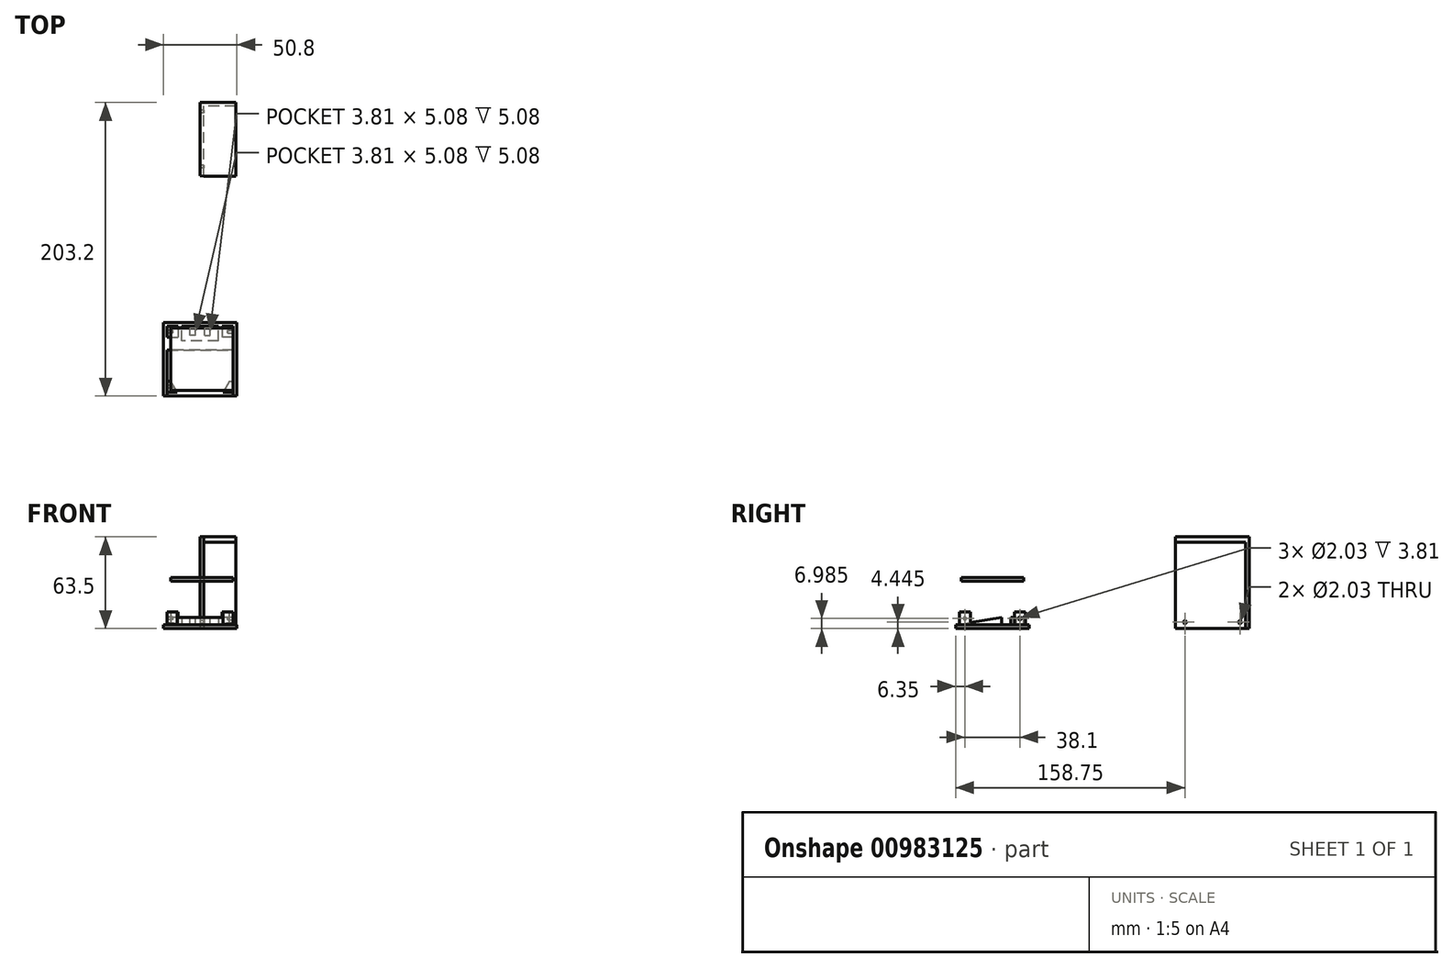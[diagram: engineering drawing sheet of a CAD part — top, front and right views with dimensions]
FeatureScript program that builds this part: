
annotation { "Feature Type Name" : "Feature", "Feature Type Description" : "" }
export const myFeature = defineFeature(function(context is Context, id is Id, definition is map)
    precondition{}
    {
        {
            var Q0;
            Q0=qCreatedBy(makeId("Top.planeOp"),FACE);
            var sketch = newSketch(context, id + "F0", { "sketchPlane" : qUnion([Q0])});
            skLineSegment(sketch, "E0.bottom", {"start": v(25.4, 25.4) * mm, "end": v(-25.4, 25.4) * mm});
            skLineSegment(sketch, "E0.top", {"start": v(25.4, -25.4) * mm, "end": v(-25.4, -25.4) * mm});
            skLineSegment(sketch, "E0.left", {"start": v(25.4, 25.4) * mm, "end": v(25.4, -25.4) * mm});
            skLineSegment(sketch, "E0.right", {"start": v(-25.4, 25.4) * mm, "end": v(-25.4, -25.4) * mm});
            skPoint(sketch, "E0.middle", {"position": v(0, 0) * mm});
            skSolve(sketch);
        }
        {
            var Q0;
            Q0=makeQuery(id+"F0.imprint","IMPRINT",FACE,{"disambiguationData":[TD([[makeQuery(id+"F0.imprint","IMPRINT",EDGE,{"derivedFrom":sQuery(id+"F0.wireOp",EDGE,"E0.bottom")}),1.0]])]});
            extrude(context, id + "F1", {"entities" : qUnion([Q0]), "depth" : 2.54 * mm, "offsetDistance" : 25.4 * mm});
        }
        {
            var Q0;
            Q0=makeQuery(id+"F1.opExtrude","CAP_FACE",FACE,{"disambiguationData":[OSD([sQuery(id+"F0.wireOp",EDGE,"E0.bottom"),sQuery(id+"F0.wireOp",EDGE,"E0.top"),sQuery(id+"F0.wireOp",EDGE,"E0.left"),sQuery(id+"F0.wireOp",EDGE,"E0.right")])],"isStart":false});
            var sketch = newSketch(context, id + "F2", { "sketchPlane" : qUnion([Q0])});
            skLineSegment(sketch, "E1", {"start": v(0, 25.4) * mm, "end": v(0, 12.7) * mm});
            skLineSegment(sketch, "E2.bottom", {"start": v(0, 12.7) * mm, "end": v(12.7, 12.7) * mm});
            skLineSegment(sketch, "E2.top", {"start": v(0, 25.4) * mm, "end": v(12.7, 25.4) * mm});
            skLineSegment(sketch, "E2.left", {"start": v(0, 12.7) * mm, "end": v(0, 25.4) * mm});
            skLineSegment(sketch, "E2.right", {"start": v(12.7, 12.7) * mm, "end": v(12.7, 25.4) * mm});
            skLineSegment(sketch, "E3.bottom", {"start": v(0, 12.7) * mm, "end": v(-12.7, 12.7) * mm});
            skLineSegment(sketch, "E3.top", {"start": v(0, 25.4) * mm, "end": v(-12.7, 25.4) * mm});
            skLineSegment(sketch, "E3.right", {"start": v(-12.7, 12.7) * mm, "end": v(-12.7, 25.4) * mm});
            skSolve(sketch);
        }
        {
            var Q0;
            Q0=makeQuery(id+"F2.imprint","IMPRINT",FACE,{"disambiguationData":[TD([[makeQuery(id+"F2.imprint","IMPRINT",EDGE,{"derivedFrom":sQuery(id+"F2.wireOp",EDGE,"E3.bottom")}),-1.0]])]});
            var Q1;
            Q1=makeQuery(id+"F2.imprint","IMPRINT",FACE,{"disambiguationData":[TD([[makeQuery(id+"F2.imprint","IMPRINT",EDGE,{"derivedFrom":sQuery(id+"F2.wireOp",EDGE,"E2.bottom")}),1.0]])]});
            extrude(context, id + "F3", {"entities" : qUnion([Q0, Q1]), "operationType" : NewBodyOperationType.ADD, "depth" : 5.08 * mm, "offsetDistance" : 25.4 * mm});
        }
        {
            var Q0;
            Q0=makeQuery(id+"F3.opExtrude","CAP_FACE",FACE,{"disambiguationData":[OSD([sQuery(id+"F2.wireOp",EDGE,"E2.bottom"),sQuery(id+"F2.wireOp",EDGE,"E2.top"),sQuery(id+"F2.wireOp",EDGE,"E2.right"),sQuery(id+"F2.wireOp",EDGE,"E3.bottom"),sQuery(id+"F2.wireOp",EDGE,"E3.top"),sQuery(id+"F2.wireOp",EDGE,"E3.right")])],"isStart":false});
            var sketch = newSketch(context, id + "F4", { "sketchPlane" : qUnion([Q0])});
            skLineSegment(sketch, "E4", {"start": v(0, 25.4) * mm, "end": v(0, 16.51) * mm, "construction": true});
            skPoint(sketch, "E4.endSnap0", {"position": v(0, 12.7) * mm});
            skLineSegment(sketch, "E5", {"start": v(0, 16.51) * mm, "end": v(-3.17, 16.51) * mm, "construction": true});
            skLineSegment(sketch, "E6.bottom", {"start": v(-3.17, 16.51) * mm, "end": v(-6.99, 16.51) * mm});
            skLineSegment(sketch, "E6.top", {"start": v(-3.18, 21.6) * mm, "end": v(-6.99, 21.6) * mm});
            skLineSegment(sketch, "E6.left", {"start": v(-3.18, 16.51) * mm, "end": v(-3.18, 21.6) * mm});
            skLineSegment(sketch, "E6.right", {"start": v(-6.98, 16.51) * mm, "end": v(-6.99, 21.6) * mm});
            skLineSegment(sketch, "E7.MirrorCS", {"start": v(0, 16.51) * mm, "end": v(3.18, 16.51) * mm, "construction": true});
            skLineSegment(sketch, "E8.MirrorCS", {"start": v(3.18, 16.51) * mm, "end": v(3.18, 21.6) * mm});
            skLineSegment(sketch, "E9.MirrorCS", {"start": v(3.18, 21.6) * mm, "end": v(6.99, 21.6) * mm});
            skLineSegment(sketch, "E10.MirrorCS", {"start": v(6.99, 16.51) * mm, "end": v(6.99, 21.6) * mm});
            skLineSegment(sketch, "E11.MirrorCS", {"start": v(3.18, 16.51) * mm, "end": v(6.99, 16.51) * mm});
            skSolve(sketch);
        }
        {
            var Q0;
            Q0=makeQuery(id+"F4.imprint","IMPRINT",FACE,{"disambiguationData":[TD([[makeQuery(id+"F4.imprint","IMPRINT",EDGE,{"derivedFrom":sQuery(id+"F4.wireOp",EDGE,"E6.bottom")}),-1.0]])]});
            var Q1;
            Q1=makeQuery(id+"F4.imprint","IMPRINT",FACE,{"disambiguationData":[TD([[makeQuery(id+"F4.imprint","IMPRINT",EDGE,{"derivedFrom":sQuery(id+"F4.wireOp",EDGE,"E8.MirrorCS")}),-1.0]])]});
            extrude(context, id + "F5", {"entities" : qUnion([Q0, Q1]), "operationType" : NewBodyOperationType.REMOVE, "oppositeDirection" : true, "depth" : 5.08 * mm, "offsetDistance" : 25.4 * mm});
        }
        {
            var Q0;
            Q0=makeQuery(id+"F1.opExtrude","CAP_FACE",FACE,{"disambiguationData":[OSD([sQuery(id+"F0.wireOp",EDGE,"E0.bottom"),sQuery(id+"F0.wireOp",EDGE,"E0.top"),sQuery(id+"F0.wireOp",EDGE,"E0.left"),sQuery(id+"F0.wireOp",EDGE,"E0.right")])],"isStart":false});
            var sketch = newSketch(context, id + "F6", { "sketchPlane" : qUnion([Q0])});
            skLineSegment(sketch, "E12", {"start": v(-25.4, 22.86) * mm, "end": v(-22.86, 22.86) * mm});
            skLineSegment(sketch, "E13", {"start": v(-22.86, 22.86) * mm, "end": v(-22.86, 25.4) * mm});
            skLineSegment(sketch, "E14.MirrorCS", {"start": v(-25.4, -22.86) * mm, "end": v(-22.86, -22.86) * mm});
            skLineSegment(sketch, "E15.MirrorCS", {"start": v(-22.86, -22.86) * mm, "end": v(-22.86, -25.4) * mm});
            skLineSegment(sketch, "E16.MirrorCS", {"start": v(22.86, 22.86) * mm, "end": v(22.86, 25.4) * mm});
            skLineSegment(sketch, "E17.MirrorCS", {"start": v(25.4, 22.86) * mm, "end": v(22.86, 22.86) * mm});
            skLineSegment(sketch, "E18.MirrorCS", {"start": v(25.4, -22.86) * mm, "end": v(22.86, -22.86) * mm});
            skLineSegment(sketch, "E19.MirrorCS", {"start": v(22.86, -22.86) * mm, "end": v(22.86, -25.4) * mm});
            skLineSegment(sketch, "E20.bottom", {"start": v(-22.86, 22.86) * mm, "end": v(-15.24, 22.86) * mm});
            skLineSegment(sketch, "E20.top", {"start": v(-22.86, 15.24) * mm, "end": v(-15.24, 15.24) * mm});
            skLineSegment(sketch, "E20.left", {"start": v(-22.86, 22.86) * mm, "end": v(-22.86, 15.24) * mm});
            skLineSegment(sketch, "E20.right", {"start": v(-15.24, 22.86) * mm, "end": v(-15.24, 15.24) * mm});
            skLineSegment(sketch, "E21.MirrorCS", {"start": v(22.86, 22.86) * mm, "end": v(15.24, 22.86) * mm});
            skLineSegment(sketch, "E22.MirrorCS", {"start": v(15.24, 22.86) * mm, "end": v(15.24, 15.24) * mm});
            skLineSegment(sketch, "E23.MirrorCS", {"start": v(22.86, 22.86) * mm, "end": v(22.86, 15.24) * mm});
            skLineSegment(sketch, "E24.MirrorCS", {"start": v(22.86, 15.24) * mm, "end": v(15.24, 15.24) * mm});
            skLineSegment(sketch, "E25.bottom", {"start": v(-22.86, -25.4) * mm, "end": v(22.86, -25.4) * mm});
            skLineSegment(sketch, "E25.top", {"start": v(-22.86, 6.35) * mm, "end": v(22.86, 6.35) * mm});
            skLineSegment(sketch, "E25.left", {"start": v(-22.86, -25.4) * mm, "end": v(-22.86, 6.35) * mm});
            skLineSegment(sketch, "E25.right", {"start": v(22.86, -25.4) * mm, "end": v(22.86, 6.35) * mm});
            skLineSegment(sketch, "E26.MirrorCS", {"start": v(-22.86, -22.86) * mm, "end": v(-22.86, -15.24) * mm});
            skLineSegment(sketch, "E27.MirrorCS", {"start": v(22.86, -22.86) * mm, "end": v(22.86, -15.24) * mm});
            skLineSegment(sketch, "E28.MirrorCS", {"start": v(22.86, -22.86) * mm, "end": v(15.24, -22.86) * mm});
            skLineSegment(sketch, "E29.MirrorCS", {"start": v(22.86, -15.24) * mm, "end": v(15.24, -15.24) * mm});
            skLineSegment(sketch, "E30.MirrorCS", {"start": v(15.24, -22.86) * mm, "end": v(15.24, -15.24) * mm});
            skLineSegment(sketch, "E31.MirrorCS", {"start": v(-22.86, -15.24) * mm, "end": v(-15.24, -15.24) * mm});
            skLineSegment(sketch, "E32.MirrorCS", {"start": v(-15.24, -22.86) * mm, "end": v(-15.24, -15.24) * mm});
            skLineSegment(sketch, "E33.MirrorCS", {"start": v(-22.86, -22.86) * mm, "end": v(-15.24, -22.86) * mm});
            skSolve(sketch);
        }
        {
            var Q0;
            Q0=makeQuery(id+"F6.imprint","IMPRINT",FACE,{"disambiguationData":[TD([[makeQuery(id+"F6.imprint","IMPRINT",EDGE,{"derivedFrom":sQuery(id+"F6.wireOp",EDGE,"E20.bottom")}),-1.0]])]});
            var Q1;
            Q1=makeQuery(id+"F6.imprint","IMPRINT",FACE,{"disambiguationData":[TD([[makeQuery(id+"F6.imprint","IMPRINT",EDGE,{"derivedFrom":sQuery(id+"F6.wireOp",EDGE,"E21.MirrorCS")}),1.0]])]});
            var Q2;
            {var subQ3=sQuery(id+"F6.wireOp",EDGE,"E25.bottom");Q2=makeQuery(id+"F6.imprint","IMPRINT",FACE,{"disambiguationData":[TD([[makeQuery(id+"F6.imprint","IMPRINT",EDGE,{"derivedFrom":subQ3}),-1.0]])]});}
            extrude(context, id + "F7", {"entities" : qUnion([Q0, Q1, Q2]), "operationType" : NewBodyOperationType.ADD, "depth" : 8.9 * mm, "offsetDistance" : 25.4 * mm});
        }
        {
            var Q0;
            Q0=makeQuery(id+"F7.opExtrude","CAP_EDGE",EDGE,{"disambiguationData":[OSD([sQuery(id+"F6.wireOp",EDGE,"E25.bottom")])],"isStart":false});
            chamfer(context, id + "F8", {"entities" : qUnion([Q0]), "chamferType" : ChamferType.OFFSET_ANGLE, "width" : 8.9 * mm, "oppositeDirection" : false, "angle" : 81 * degree, "tangentPropagation" : true});
        }
        {
            var Q0;
            Q0=qCreatedBy(makeId("Top.planeOp"),FACE);
            var sketch = newSketch(context, id + "F9", { "sketchPlane" : qUnion([Q0])});
            skLineSegment(sketch, "E34", {"start": v(0, 0) * mm, "end": v(0, 127) * mm, "construction": true});
            skLineSegment(sketch, "E35", {"start": v(0, 127) * mm, "end": v(0, 177.8) * mm});
            skLineSegment(sketch, "E36", {"start": v(0, 177.8) * mm, "end": v(24.64, 177.8) * mm});
            skLineSegment(sketch, "E37", {"start": v(24.64, 177.8) * mm, "end": v(24.64, 175.26) * mm});
            skLineSegment(sketch, "E38", {"start": v(24.64, 175.26) * mm, "end": v(2.54, 175.26) * mm});
            skLineSegment(sketch, "E39", {"start": v(2.54, 175.26) * mm, "end": v(2.54, 126.89) * mm});
            skLineSegment(sketch, "E40", {"start": v(2.54, 126.89) * mm, "end": v(0, 127) * mm});
            skSolve(sketch);
        }
        {
            var Q0;
            Q0=makeQuery(id+"F9.imprint","IMPRINT",FACE,{"disambiguationData":[TD([[makeQuery(id+"F9.imprint","IMPRINT",EDGE,{"derivedFrom":sQuery(id+"F9.wireOp",EDGE,"E35")}),-1.0]])]});
            extrude(context, id + "F10", {"entities" : qUnion([Q0]), "depth" : 63.5 * mm, "offsetDistance" : 25.4 * mm});
        }
        {
            var Q0;
            Q0=makeQuery(id+"F10.opExtrude","SWEPT_FACE",FACE,{"disambiguationData":[OSD([sQuery(id+"F9.wireOp",EDGE,"E39")])]});
            var sketch = newSketch(context, id + "F11", { "sketchPlane" : qUnion([Q0])});
            skLineSegment(sketch, "E41", {"start": v(126.89, 63.5) * mm, "end": v(126.89, 59.69) * mm});
            skLineSegment(sketch, "E42.bottom", {"start": v(126.89, 59.69) * mm, "end": v(175.26, 59.69) * mm});
            skLineSegment(sketch, "E42.top", {"start": v(126.89, 63.5) * mm, "end": v(175.26, 63.5) * mm});
            skLineSegment(sketch, "E42.left", {"start": v(126.89, 59.69) * mm, "end": v(126.89, 63.5) * mm});
            skLineSegment(sketch, "E42.right", {"start": v(175.26, 59.69) * mm, "end": v(175.26, 63.5) * mm});
            skSolve(sketch);
        }
        {
            var Q0;
            Q0=makeQuery(id+"F11.imprint","IMPRINT",FACE,{"disambiguationData":[TD([[makeQuery(id+"F11.imprint","IMPRINT",EDGE,{"derivedFrom":sQuery(id+"F11.wireOp",EDGE,"E42.bottom")}),1.0]])]});
            extrude(context, id + "F12", {"entities" : qUnion([Q0]), "operationType" : NewBodyOperationType.ADD, "depth" : 22.1 * mm, "offsetDistance" : 25.4 * mm});
        }
        {
            var Q0;
            Q0=makeQuery(id+"F1.opExtrude","CAP_FACE",FACE,{"disambiguationData":[OSD([sQuery(id+"F0.wireOp",EDGE,"E0.bottom"),sQuery(id+"F0.wireOp",EDGE,"E0.top"),sQuery(id+"F0.wireOp",EDGE,"E0.left"),sQuery(id+"F0.wireOp",EDGE,"E0.right")])],"isStart":false});
            var sketch = newSketch(context, id + "F13", { "sketchPlane" : qUnion([Q0])});
            skLineSegment(sketch, "E43.bottom", {"start": v(-15.24, -15.24) * mm, "end": v(-22.86, -15.24) * mm});
            skLineSegment(sketch, "E43.top", {"start": v(-15.24, -22.86) * mm, "end": v(-22.86, -22.86) * mm});
            skLineSegment(sketch, "E43.left", {"start": v(-15.24, -15.24) * mm, "end": v(-15.24, -22.86) * mm});
            skLineSegment(sketch, "E43.right", {"start": v(-22.86, -15.24) * mm, "end": v(-22.86, -22.86) * mm});
            skLineSegment(sketch, "E44.bottom", {"start": v(15.24, -15.24) * mm, "end": v(22.86, -15.24) * mm});
            skLineSegment(sketch, "E44.top", {"start": v(15.24, -22.86) * mm, "end": v(22.86, -22.86) * mm});
            skLineSegment(sketch, "E44.left", {"start": v(15.24, -15.24) * mm, "end": v(15.24, -22.86) * mm});
            skLineSegment(sketch, "E44.right", {"start": v(22.86, -15.24) * mm, "end": v(22.86, -22.86) * mm});
            skSolve(sketch);
        }
        {
            var Q0;
            Q0=makeQuery(id+"F13.imprint","IMPRINT",FACE,{"disambiguationData":[TD([[makeQuery(id+"F13.imprint","IMPRINT",EDGE,{"derivedFrom":sQuery(id+"F13.wireOp",EDGE,"E43.bottom")}),-1.0]])]});
            var Q1;
            Q1=makeQuery(id+"F13.imprint","IMPRINT",FACE,{"disambiguationData":[TD([[makeQuery(id+"F13.imprint","IMPRINT",EDGE,{"derivedFrom":sQuery(id+"F13.wireOp",EDGE,"E44.bottom")}),1.0]])]});
            extrude(context, id + "F14", {"entities" : qUnion([Q0, Q1]), "operationType" : NewBodyOperationType.ADD, "depth" : 8.9 * mm, "offsetDistance" : 25.4 * mm});
        }
        {
            var Q0;
            Q0=makeQuery(id+"F7.opExtrude","SWEPT_FACE",FACE,{"disambiguationData":[OSD([sQuery(id+"F6.wireOp",EDGE,"E20.left")])]});
            var sketch = newSketch(context, id + "F15", { "sketchPlane" : qUnion([Q0])});
            skLineSegment(sketch, "E45", {"start": v(-22.86, 6.99) * mm, "end": v(-15.24, 6.99) * mm, "construction": true});
            skCircle(sketch, "E46", {"center": v(-19.05, 6.99) * mm, "radius": 1.02 * mm});
            skLineSegment(sketch, "E47.MirrorCS", {"start": v(22.86, 6.99) * mm, "end": v(15.24, 6.99) * mm, "construction": true});
            skCircle(sketch, "E48.MirrorC", {"center": v(19.05, 6.99) * mm, "radius": 1.02 * mm});
            skSolve(sketch);
        }
        {
            var Q0;
            Q0=makeQuery(id+"F7.opExtrude","SWEPT_FACE",FACE,{"disambiguationData":[OSD([sQuery(id+"F6.wireOp",EDGE,"E23.MirrorCS")])]});
            var sketch = newSketch(context, id + "F16", { "sketchPlane" : qUnion([Q0])});
            skLineSegment(sketch, "E49", {"start": v(15.24, 6.99) * mm, "end": v(22.86, 6.99) * mm, "construction": true});
            skCircle(sketch, "E50", {"center": v(19.05, 6.99) * mm, "radius": 1.02 * mm});
            skLineSegment(sketch, "E51.MirrorCS", {"start": v(-15.24, 6.99) * mm, "end": v(-22.86, 6.99) * mm, "construction": true});
            skCircle(sketch, "E52.MirrorC", {"center": v(-19.05, 6.99) * mm, "radius": 1.02 * mm});
            skSolve(sketch);
        }
        {
            var Q0;
            Q0=makeQuery(id+"F16.imprint","IMPRINT",FACE,{"disambiguationData":[TD([[makeQuery(id+"F16.imprint","IMPRINT",EDGE,{"derivedFrom":sQuery(id+"F16.wireOp",EDGE,"E52.MirrorC")}),-1.0]])]});
            var Q1;
            Q1=makeQuery(id+"F16.imprint","IMPRINT",FACE,{"disambiguationData":[TD([[makeQuery(id+"F16.imprint","IMPRINT",EDGE,{"derivedFrom":sQuery(id+"F16.wireOp",EDGE,"E50")}),1.0]])]});
            extrude(context, id + "F17", {"entities" : qUnion([Q0, Q1]), "operationType" : NewBodyOperationType.REMOVE, "oppositeDirection" : true, "depth" : 3.8 * mm, "offsetDistance" : 25.4 * mm});
        }
        {
            var Q0;
            Q0 = qSketchRegion(id + "F15", true);
            extrude(context, id + "F18", {"entities" : qUnion([Q0]), "operationType" : NewBodyOperationType.REMOVE, "oppositeDirection" : true, "depth" : 3.8 * mm, "offsetDistance" : 25.4 * mm});
        }
        {
            var Q0;
            Q0=makeQuery(id+"F14.opExtrude","SWEPT_EDGE",EDGE,{"disambiguationData":[OSD([sQuery(id+"F13.wireOp",EDGE,"E43.bottom"),sQuery(id+"F13.wireOp",EDGE,"E43.left")])]});
            chamfer(context, id + "F19", {"entities" : qUnion([Q0]), "chamferType" : ChamferType.OFFSET_ANGLE, "width" : 5.08 * mm, "oppositeDirection" : false, "angle" : 60 * degree, "tangentPropagation" : true});
        }
        {
            var Q0;
            Q0=makeQuery(id+"F14.opExtrude","SWEPT_EDGE",EDGE,{"disambiguationData":[OSD([sQuery(id+"F13.wireOp",EDGE,"E44.bottom"),sQuery(id+"F13.wireOp",EDGE,"E44.left")])]});
            chamfer(context, id + "F20", {"entities" : qUnion([Q0]), "chamferType" : ChamferType.OFFSET_ANGLE, "width" : 5.08 * mm, "oppositeDirection" : true, "angle" : 60 * degree, "tangentPropagation" : true});
        }
        {
            var Q0;
            Q0=makeQuery(id+"F3.boolean.opBoolean","MERGE",FACE,{"derivedFrom":[makeQuery(id+"F1.opExtrude","SWEPT_FACE",FACE,{"disambiguationData":[OSD([sQuery(id+"F0.wireOp",EDGE,"E0.bottom")])]}),makeQuery(id+"F3.opExtrude","SWEPT_FACE",FACE,{"disambiguationData":[OSD([sQuery(id+"F2.wireOp",EDGE,"E2.top"),sQuery(id+"F2.wireOp",EDGE,"E3.top")])]})]});
            var sketch = newSketch(context, id + "F21", { "sketchPlane" : qUnion([Q0])});
            skLineSegment(sketch, "E53.bottom", {"start": v(-12.7, 7.62) * mm, "end": v(12.7, 7.62) * mm});
            skLineSegment(sketch, "E53.top", {"start": v(-12.7, 2.54) * mm, "end": v(12.7, 2.54) * mm});
            skLineSegment(sketch, "E53.left", {"start": v(-12.7, 7.62) * mm, "end": v(-12.7, 2.54) * mm});
            skLineSegment(sketch, "E53.right", {"start": v(12.7, 7.62) * mm, "end": v(12.7, 2.54) * mm});
            skSolve(sketch);
        }
        {
            var Q0;
            Q0=makeQuery(id+"F21.imprint","IMPRINT",FACE,{"disambiguationData":[TD([[makeQuery(id+"F21.imprint","IMPRINT",EDGE,{"derivedFrom":sQuery(id+"F21.wireOp",EDGE,"E53.bottom")}),-1.0]])]});
            extrude(context, id + "F22", {"entities" : qUnion([Q0]), "operationType" : NewBodyOperationType.REMOVE, "oppositeDirection" : true, "depth" : 2.54 * mm, "offsetDistance" : 25.4 * mm});
        }
        {
            var Q0;
            Q0=makeQuery(id+"F10.opExtrude","SWEPT_FACE",FACE,{"disambiguationData":[OSD([sQuery(id+"F9.wireOp",EDGE,"E35")])]});
            var sketch = newSketch(context, id + "F23", { "sketchPlane" : qUnion([Q0])});
            skLineSegment(sketch, "E54", {"start": v(-177.8, 0) * mm, "end": v(-175.26, 0) * mm});
            skLineSegment(sketch, "E55", {"start": v(-175.26, 0) * mm, "end": v(-175.26, 8.89) * mm});
            skLineSegment(sketch, "E56.bottom", {"start": v(-175.26, 8.89) * mm, "end": v(-167.64, 8.89) * mm});
            skLineSegment(sketch, "E56.top", {"start": v(-175.26, 0) * mm, "end": v(-167.64, 0) * mm});
            skLineSegment(sketch, "E56.left", {"start": v(-175.26, 8.89) * mm, "end": v(-175.26, 0) * mm});
            skLineSegment(sketch, "E56.right", {"start": v(-167.64, 8.9) * mm, "end": v(-167.64, 0) * mm});
            skLineSegment(sketch, "E57", {"start": v(-127, 0) * mm, "end": v(-129.54, 0) * mm});
            skLineSegment(sketch, "E58.bottom", {"start": v(-129.54, 0) * mm, "end": v(-137.16, 0) * mm});
            skLineSegment(sketch, "E58.top", {"start": v(-129.54, 8.89) * mm, "end": v(-137.16, 8.89) * mm});
            skLineSegment(sketch, "E58.left", {"start": v(-129.54, 0) * mm, "end": v(-129.54, 8.89) * mm});
            skLineSegment(sketch, "E58.right", {"start": v(-137.16, 0) * mm, "end": v(-137.16, 8.9) * mm});
            skLineSegment(sketch, "E59", {"start": v(-175.26, 4.44) * mm, "end": v(-167.64, 4.45) * mm, "construction": true});
            skLineSegment(sketch, "E60", {"start": v(-137.16, 4.45) * mm, "end": v(-129.54, 4.44) * mm, "construction": true});
            skCircle(sketch, "E61", {"center": v(-171.45, 4.44) * mm, "radius": 1.02 * mm});
            skCircle(sketch, "E62", {"center": v(-133.35, 4.44) * mm, "radius": 1.02 * mm});
            skSolve(sketch);
        }
        {
            var Q0;
            Q0=makeQuery(id+"F23.imprint","IMPRINT",FACE,{"disambiguationData":[TD([[makeQuery(id+"F23.imprint","IMPRINT",EDGE,{"derivedFrom":sQuery(id+"F23.wireOp",EDGE,"E61")}),1.0]])]});
            var Q1;
            Q1=makeQuery(id+"F23.imprint","IMPRINT",FACE,{"disambiguationData":[TD([[makeQuery(id+"F23.imprint","IMPRINT",EDGE,{"derivedFrom":sQuery(id+"F23.wireOp",EDGE,"E62")}),1.0]])]});
            extrude(context, id + "F24", {"entities" : qUnion([Q0, Q1]), "operationType" : NewBodyOperationType.REMOVE, "oppositeDirection" : true, "depth" : 5.08 * mm, "offsetDistance" : 25.4 * mm});
        }
        {
            var Q0;
            Q0=qCreatedBy(makeId("Top.planeOp"),FACE);
            var sketch = newSketch(context, id + "F25", { "sketchPlane" : qUnion([Q0])});
            skLineSegment(sketch, "E63", {"start": v(0, 0) * mm, "end": v(88.9, 0) * mm, "construction": true});
            skLineSegment(sketch, "E64", {"start": v(88.9, 0) * mm, "end": v(88.9, 25.4) * mm});
            skLineSegment(sketch, "E65.bottom", {"start": v(88.9, 25.4) * mm, "end": v(139.7, 25.4) * mm});
            skLineSegment(sketch, "E65.top", {"start": v(88.9, -25.4) * mm, "end": v(139.7, -25.4) * mm});
            skLineSegment(sketch, "E65.left", {"start": v(88.9, 25.4) * mm, "end": v(88.9, -25.4) * mm});
            skLineSegment(sketch, "E65.right", {"start": v(139.7, 25.4) * mm, "end": v(139.7, -25.4) * mm});
            skLineSegment(sketch, "E66", {"start": v(91.44, 25.4) * mm, "end": v(91.44, 22.86) * mm});
            skLineSegment(sketch, "E67", {"start": v(91.44, 22.86) * mm, "end": v(88.9, 22.86) * mm});
            skLineSegment(sketch, "E68.bottom", {"start": v(91.44, 22.86) * mm, "end": v(137.16, 22.86) * mm});
            skLineSegment(sketch, "E68.top", {"start": v(91.44, -22.86) * mm, "end": v(137.16, -22.86) * mm});
            skLineSegment(sketch, "E68.left", {"start": v(91.44, 22.86) * mm, "end": v(91.44, -22.86) * mm});
            skLineSegment(sketch, "E68.right", {"start": v(137.16, 22.86) * mm, "end": v(137.16, -22.86) * mm});
            skLineSegment(sketch, "E69", {"start": v(91.44, 22.86) * mm, "end": v(92.71, 22.86) * mm});
            skLineSegment(sketch, "E70", {"start": v(92.71, 22.86) * mm, "end": v(92.71, 21.59) * mm});
            skLineSegment(sketch, "E71", {"start": v(92.71, 21.59) * mm, "end": v(91.44, 21.59) * mm});
            skLineSegment(sketch, "E72", {"start": v(91.44, 21.59) * mm, "end": v(92.71, 21.59) * mm});
            skLineSegment(sketch, "E73", {"start": v(137.16, 22.86) * mm, "end": v(135.9, 22.86) * mm});
            skLineSegment(sketch, "E74", {"start": v(135.9, 22.86) * mm, "end": v(135.9, 21.6) * mm});
            skLineSegment(sketch, "E75", {"start": v(135.9, 21.6) * mm, "end": v(137.16, 21.6) * mm});
            skLineSegment(sketch, "E76.bottom", {"start": v(92.71, 21.59) * mm, "end": v(135.9, 21.59) * mm});
            skLineSegment(sketch, "E76.top", {"start": v(92.71, -21.59) * mm, "end": v(135.9, -21.59) * mm});
            skLineSegment(sketch, "E76.left", {"start": v(92.71, 21.59) * mm, "end": v(92.71, -21.59) * mm});
            skLineSegment(sketch, "E76.right", {"start": v(135.9, 21.6) * mm, "end": v(135.9, -21.59) * mm});
            skSolve(sketch);
        }
        {
            var Q0;
            Q0=makeQuery(id+"F25.imprint","IMPRINT",FACE,{"disambiguationData":[TD([[makeQuery(id+"F25.imprint","IMPRINT",EDGE,{"derivedFrom":sQuery(id+"F25.wireOp",EDGE,"E76.bottom")}),-1.0]])]});
            extrude(context, id + "F26", {"entities" : qUnion([Q0]), "depth" : 2.54 * mm, "offsetDistance" : 25.4 * mm});
        }
        {
            var Q0;
            Q0=makeQuery(id+"F26.opExtrude","SWEPT_BODY",BODY,{"disambiguationData":[OSD([sQuery(id+"F25.wireOp",EDGE,"E76.bottom"),sQuery(id+"F25.wireOp",EDGE,"E76.top"),sQuery(id+"F25.wireOp",EDGE,"E76.left"),sQuery(id+"F25.wireOp",EDGE,"E76.right")])]});
            transform(context, id + "F27", {"entities" : qUnion([Q0]), "transformType" : TransformType.TRANSLATION_3D, "dx" : -113.03 * mm, "dy" : 0 * mm, "dz" : 32.77 * mm, "makeCopy" : false});
        }
    });
